# Revit family: Carrier_Closet_Offset_Vertical_Left_Hand-Zurn-Z1209-ND4
name_source: partatom
category: Plumbing Fixtures
units: mm (PartAtom-declared; Revit-internal decimal feet)

## family parameters
Always vertical = Yes
Cut with Voids When Loaded = No
Maintain Annotation Orientation = No
OmniClass Number = 23.45.55.11
OmniClass Title = Sanitary Components
Part Type = Normal
Room Calculation Point = No
Round Connector Dimension = Use Radius
Shared = No
Work Plane-Based = No

## types (1)
- Z1209-ND
    Approx. Weight (Lbs) = 109 "
    CW Connection = No
    CWFU = 0
    Connector Ditance from Leg Center = 4.25 "
    Coupling Material = ABS - Zurn - Plastic
    Coupling Radius = 2 "
    Default Elevation = 2.375 "
    Description = VERTICAL OFFSET SIPHON JET WATER CLOSET SUPPORT SYSTEM NO-HUB SERIES
    Dimension - B = 24 "
    Dimension - E = 4.125 "
    Dimension - N = 8.25 "
    HW Connection = No
    HWFU = 0
    Height = 16.75 "
    Horizontal Pipe_NL4 = No
    Horizontal Pipe_NR4 = Yes
    Main Material = Iron - Zurn - Cast - Painted - Blue
    Manufacturer = Zurn Water, LLC
    Manufacurer Brand = Zurn
    Masking region_NL4 = No
    Masking region_NR4 = Yes
    Model = Z1209-N
    Model Lines_NL4 = No
    Model lines_NR4 = Yes
    Modified Date = 11/04/2025
    Outlet Pipe Radius (Inside) = 2.013 "
    Outlet Pipe Radius (Nominal) = 2 "
    Outlet Pipe Radius (Outer) = 2.25 "
    Product Documentation Link = https://files.zurn.com
    Product Installation Sheet URL = https://files.zurn.com
    Product Page URL = https://www.zurn.com
    Product data url = https://www.bimobject.com
    URL = www.zurn.com
    Vent Connection = No
    Vent Pipe Radius (Inside) = 1.034 "
    Vent Pipe Radius (Nominal) = 1 "
    Vent Pipe Radius (Outer) = 1.188 "
    Vent_NL4 = No
    Vent_NR4 = Yes
    Vertical Offset Pipe_NL4 = No
    Vertical Offset Pipe_NR4 = Yes
    WFU = 1
    Waste Connection = Yes
    Width = 18.875 "

## geometry (parser evidence)
native form markers: Sweep x4
no freeform markers — native parametric forms only
